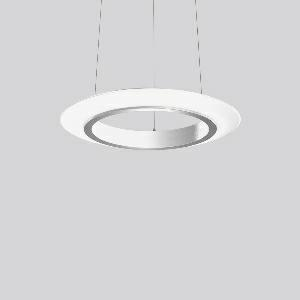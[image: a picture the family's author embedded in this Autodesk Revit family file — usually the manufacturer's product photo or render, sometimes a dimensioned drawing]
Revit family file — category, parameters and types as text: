
# Revit family: ring_of_fire_p_311669_004_2_730_f79b
name_source: partatom
category: Lighting Fixtures
units: mm (PartAtom-declared; Revit-internal decimal feet)

## family parameters
Cut with Voids When Loaded = No
Host = Face
Light Source = No
Part Type = Normal
Room Calculation Point = No
Round Connector Dimension = Use Diameter
Shared = No

## types (1)
- TuneableWhite 846 (1 x LED Modul 846, 2250 lm, 4600)
    Apparent Load = 31 VA
    CIE Flux Codes = 43 72 90 57 100
    Color Rendering = 80
    Color Temperature = 4600
    Default Elevation = 1800 mm
    Description = Series: RING OF FIRE
A uniquely shaped pendant luminaire with elliptical glass. Supporting ring made of anodised aluminium. Canopy aluminium anodised. Opal glass: mouth-blown, satin finish. Tunable white dynamically adjustable from 2700 K to 6500 K. Suitable for pendant. 3-point steel cable suspension, steplessly adjustable. Special lengths available on request. Power supply through separate cable. Converter integrated in the canopy. With Casambi smart+free Bluetooth control for wireless network and operation using Android / iOS devices, free app available for download. 
Colour: anodised aluminium
Diameter: 495 mm
Height: 55 mm
Suspension length: 500-1200 mm
Lamp: LED
Socket: without socket
Colour temperature: 2700K - 6500K
Colour rendering index (CRI): 80
System power: 31 W
Rated luminous flux: 2250 lm
Luminous efficiency: 73 lm/W
System power 2: 30 W
Rated luminous flux 2: 2100 lm
Luminous efficiency 2: 70 lm/W
System power 3: 29 W
Rated luminous flux 3: 2100 lm
Luminous efficiency 3: 72 lm/W
Control gear: Dimmable Bluetooth converter
Protection class: I
Type of protection: IP 20
    Height = 55 mm
    Lamp = 1 x LED Modul 846
    Lamp Light Flux = 2250 lm
    Lamp count = 1
    Length = 495 mm
    Lifetime = 50000 h
    Luminous efficacy = 73 lm/W
    Manufacturer = RZB
    ModVariant = No
    Model = 311669.004.2.730
    Mounting Place = Ceiling
    Mounting Type = Pendant
    Number of Poles = 1
    OnlyDefault = Yes
    Power Factor = 1
    Product Name = RING OF FIRE P
    Product group = Pendant luminaires
    ProductGroupID = 902
    Protection Class = Protection class I
    Protection Degree = IP 20
    RLX_Detail_Level = 1
    RLX_Emergency_Light_Flux = 0 lm
    RLX_Emergency_Type = 0
    RLX_Emergency_Type_DB = No
    RlxData = <blob elided: 38989 chars, md5=79e8c2af>
    Socket = socket
    Standby Power = 0 W
    System Light Flux = 2250 lm
    System Power = 31 W
    Type Comments = TuneableWhite 846
    Type Image = 311669.004.jpg
    URL = http://relux.com
    VarID = tuneablewhite_846
    Voltage = 230 V
    Voltage Range = 220-240 V
    Weight = 0.00 kg
    Width = 0 mm  [stored 0 ft]

note: [stored X ft] marks values corroborated as IEEE doubles in the binary element streams (Revit-internal decimal feet)

## geometry (parser evidence)
native form markers: Blend x4, Sweep x10
no freeform markers — native parametric forms only
